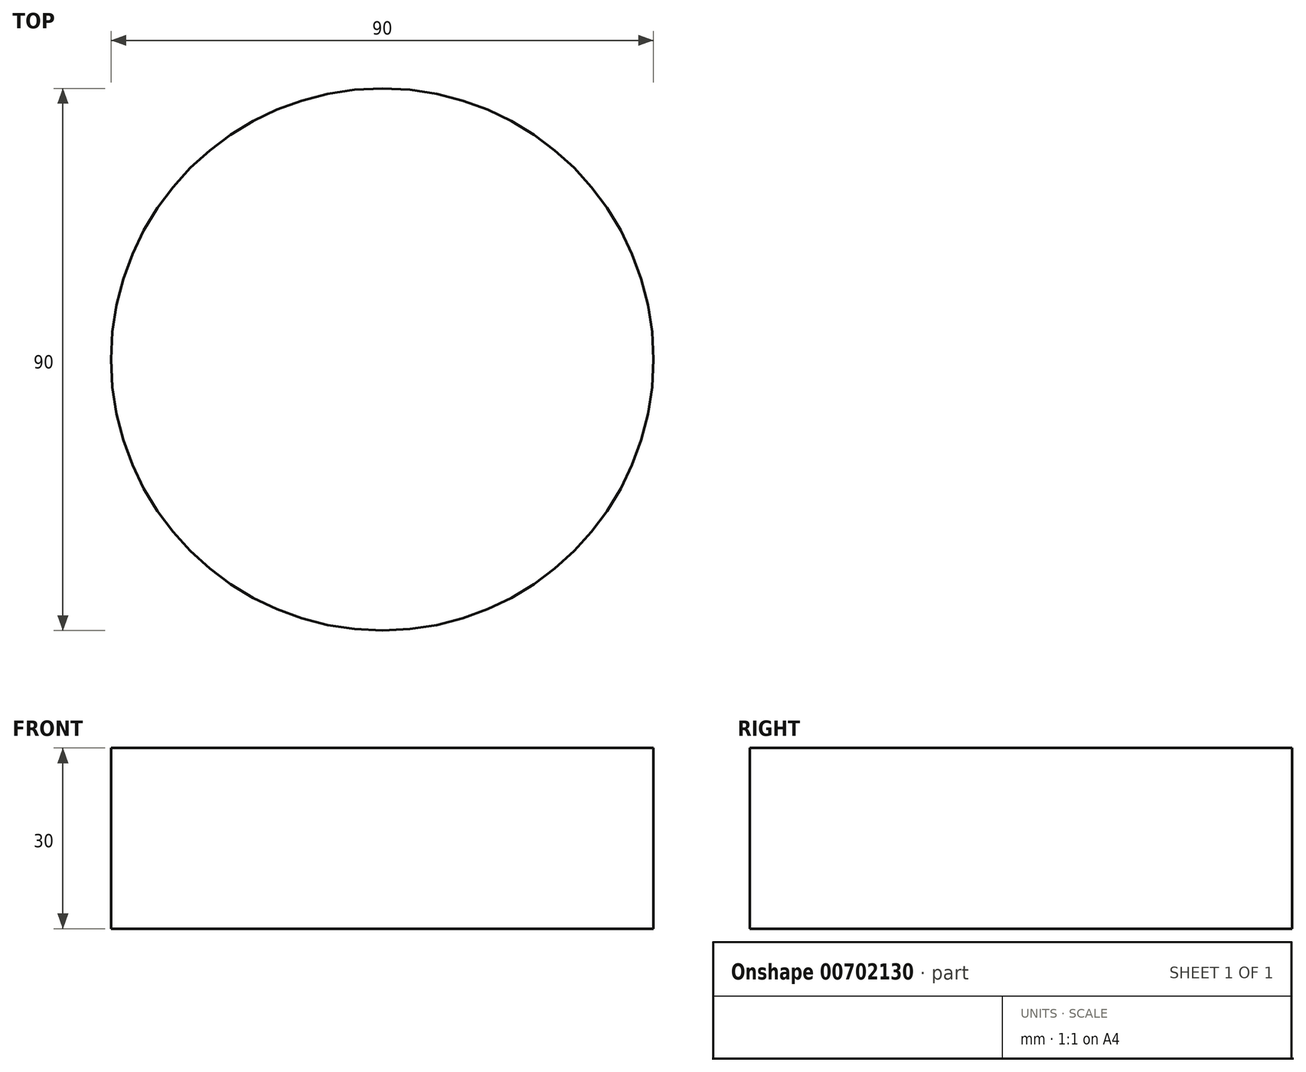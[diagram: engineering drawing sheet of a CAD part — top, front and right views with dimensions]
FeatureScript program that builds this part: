
annotation { "Feature Type Name" : "Feature", "Feature Type Description" : "" }
export const myFeature = defineFeature(function(context is Context, id is Id, definition is map)
    precondition{}
    {
        {
            var Q0;
            Q0=qCreatedBy(makeId("Top.planeOp"),FACE);
            var sketch = newSketch(context, id + "F0", { "sketchPlane" : qUnion([Q0])});
            skCircle(sketch, "E0", {"center": v(0, 0) * mm, "radius": 45 * mm});
            skSolve(sketch);
        }
        {
            var Q0;
            Q0=makeQuery(id+"F0.imprint","IMPRINT",FACE,{"disambiguationData":[TD([[makeQuery(id+"F0.imprint","IMPRINT",EDGE,{"derivedFrom":sQuery(id+"F0.wireOp",EDGE,"E0")}),1.0]])]});
            extrude(context, id + "F1", {"entities" : qUnion([Q0]), "depth" : 30 * mm, "offsetDistance" : 25 * mm});
        }
    });
